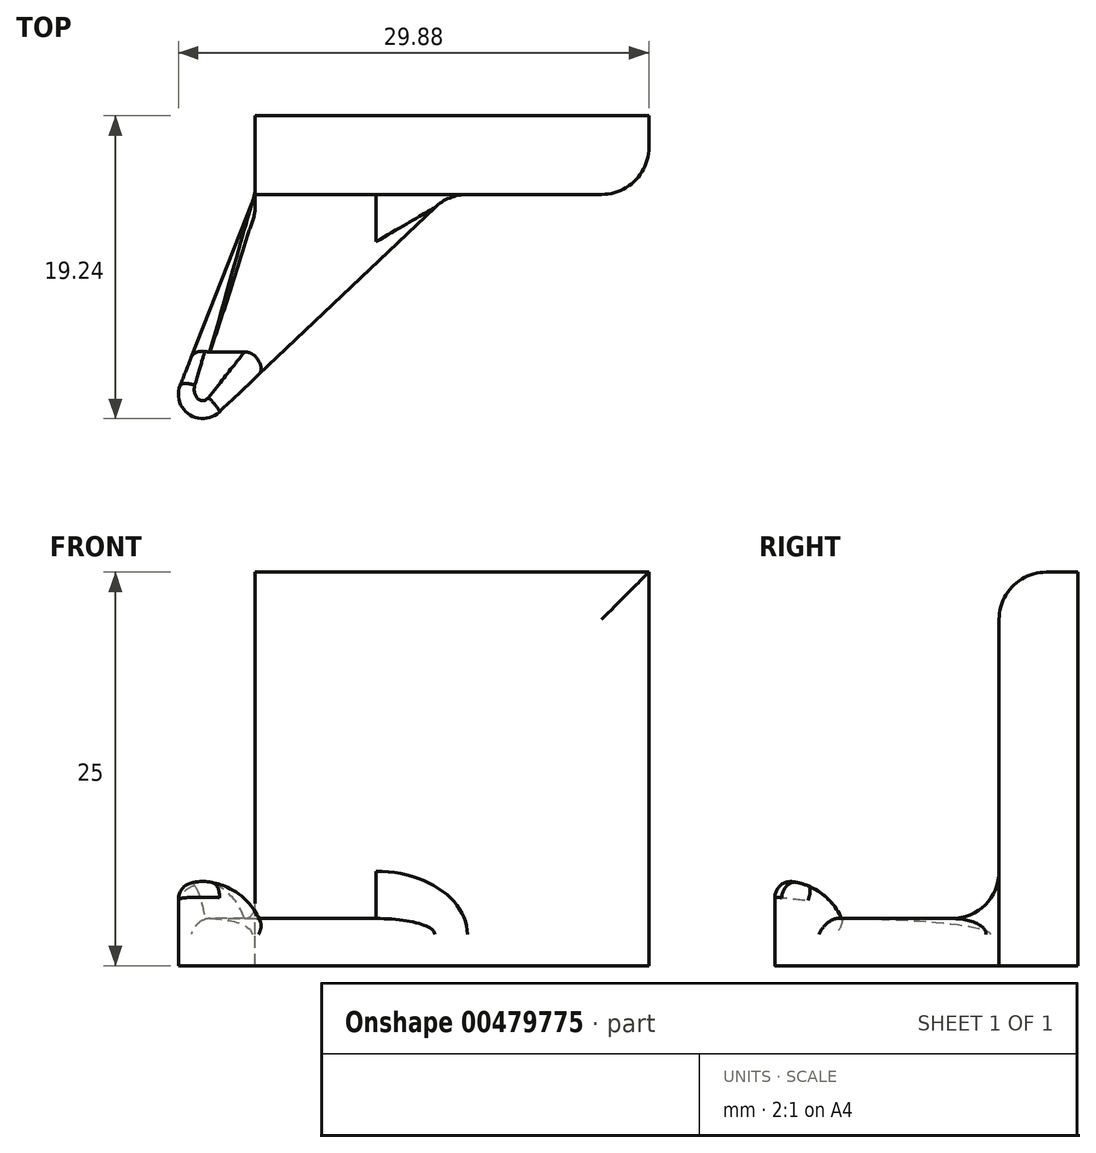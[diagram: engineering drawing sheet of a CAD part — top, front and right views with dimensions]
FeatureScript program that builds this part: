
annotation { "Feature Type Name" : "Feature", "Feature Type Description" : "" }
export const myFeature = defineFeature(function(context is Context, id is Id, definition is map)
    precondition{}
    {
        {
            var Q0;
            Q0=qCreatedBy(makeId("Front.planeOp"),FACE);
            var sketch = newSketch(context, id + "F0", { "sketchPlane" : qUnion([Q0])});
            skLineSegment(sketch, "E0.bottom", {"start": v(-12.27, 0) * mm, "end": v(12.73, 0) * mm});
            skLineSegment(sketch, "E0.top", {"start": v(-12.27, 25) * mm, "end": v(12.73, 25) * mm});
            skLineSegment(sketch, "E0.left", {"start": v(-12.27, 0) * mm, "end": v(-12.27, 25) * mm});
            skLineSegment(sketch, "E0.right", {"start": v(12.73, 0) * mm, "end": v(12.73, 25) * mm});
            skSolve(sketch);
        }
        {
            var Q0;
            Q0=makeQuery(id+"F0.imprint","IMPRINT",FACE,{"disambiguationData":[TD([[makeQuery(id+"F0.imprint","IMPRINT",EDGE,{"derivedFrom":sQuery(id+"F0.wireOp",EDGE,"E0.bottom")}),1.0]])]});
            extrude(context, id + "F1", {"entities" : qUnion([Q0]), "oppositeDirection" : true, "depth" : 5 * mm});
        }
        {
            var Q0;
            Q0=makeQuery(id+"F1.opExtrude","SWEPT_FACE",FACE,{"disambiguationData":[OSD([sQuery(id+"F0.wireOp",EDGE,"E0.bottom")])]});
            var sketch = newSketch(context, id + "F2", { "sketchPlane" : qUnion([Q0])});
            skLineSegment(sketch, "E1", {"start": v(-12.27, 0) * mm, "end": v(-17.04, 12.13) * mm});
            skLineSegment(sketch, "E2", {"start": v(-14.55, 13.81) * mm, "end": v(0, 0) * mm});
            skLineSegment(sketch, "E3", {"start": v(0, 0) * mm, "end": v(-12.27, 0) * mm});
            skArc(sketch, "E4", {"start": v(-17.04, 12.13) * mm, "mid": v(-16.47, 13.97) * mm, "end": v(-14.55, 13.81) * mm});
            skSolve(sketch);
        }
        {
            var Q0;
            Q0=makeQuery(id+"F2.imprint","IMPRINT",FACE,{"disambiguationData":[TD([[makeQuery(id+"F2.imprint","IMPRINT",EDGE,{"derivedFrom":sQuery(id+"F2.wireOp",EDGE,"E1")}),-1.0]])]});
            extrude(context, id + "F3", {"entities" : qUnion([Q0]), "operationType" : NewBodyOperationType.ADD, "oppositeDirection" : true, "depth" : 10 * mm});
        }
        {
            var Q0;
            Q0=qCreatedBy(makeId("Right.planeOp"),FACE);
            var sketch = newSketch(context, id + "F4", { "sketchPlane" : qUnion([Q0])});
            skLineSegment(sketch, "E5", {"start": v(0, 11.8) * mm, "end": v(0, 3) * mm});
            skLineSegment(sketch, "E6", {"start": v(0, 3) * mm, "end": v(-10, 3) * mm});
            skLineSegment(sketch, "E7", {"start": v(-10.78, 5.38) * mm, "end": v(-15.7, 5.38) * mm});
            skLineSegment(sketch, "E8", {"start": v(-15.7, 5.38) * mm, "end": v(-15.7, 11.74) * mm});
            skLineSegment(sketch, "E9", {"start": v(-15.7, 11.74) * mm, "end": v(0, 11.8) * mm});
            skLineSegment(sketch, "E10", {"start": v(-10, 3) * mm, "end": v(-10.78, 5.38) * mm});
            skSolve(sketch);
        }
        {
            var Q0;
            Q0=makeQuery(id+"F4.imprint","IMPRINT",FACE,{"disambiguationData":[TD([[makeQuery(id+"F4.imprint","IMPRINT",EDGE,{"derivedFrom":sQuery(id+"F4.wireOp",EDGE,"E5")}),-1.0]])]});
            extrude(context, id + "F5", {"entities" : qUnion([Q0]), "operationType" : NewBodyOperationType.REMOVE, "endBound" : BoundingType.THROUGH_ALL, "oppositeDirection" : true, "depth" : 25 * mm});
        }
        {
            var Q0;
            Q0=makeQuery(id+"F5.boolean.opBoolean","COPY",EDGE,{"derivedFrom":makeQuery(id+"F5.opExtrude","SWEPT_EDGE",EDGE,{"disambiguationData":[OSD([sQuery(id+"F4.wireOp",EDGE,"E7"),sQuery(id+"F4.wireOp",EDGE,"E10")])]})});
            fillet(context, id + "F6", {"entities" : qUnion([Q0]), "radius" : 4 * mm, "tangentPropagation" : true, "allowEdgeOverflow" : false});
        }
        {
            var Q0;
            Q0=makeQuery(id+"F5.boolean.opBoolean","INTERSECT",EDGE,{"derivedFrom":[makeQuery(id+"F3.opExtrude","SWEPT_FACE",FACE,{"disambiguationData":[OSD([sQuery(id+"F2.wireOp",EDGE,"E1")])]}),makeQuery(id+"F5.opExtrude","SWEPT_FACE",FACE,{"disambiguationData":[OSD([sQuery(id+"F4.wireOp",EDGE,"E6")])]})]});
            var Q1;
            Q1=makeQuery(id+"F5.boolean.opBoolean","INTERSECT",EDGE,{"derivedFrom":[makeQuery(id+"F3.opExtrude","SWEPT_FACE",FACE,{"disambiguationData":[OSD([sQuery(id+"F2.wireOp",EDGE,"E2")])]}),makeQuery(id+"F5.opExtrude","SWEPT_FACE",FACE,{"disambiguationData":[OSD([sQuery(id+"F4.wireOp",EDGE,"E6")])]})]});
            fillet(context, id + "F7", {"entities" : qUnion([Q0, Q1]), "radius" : 1 * mm, "tangentPropagation" : true, "allowEdgeOverflow" : false});
        }
        {
            var Q0;
            Q0=makeQuery(id+"F5.boolean.opBoolean","INTERSECT",EDGE,{"derivedFrom":[makeQuery(id+"F3.opExtrude","SWEPT_FACE",FACE,{"disambiguationData":[OSD([sQuery(id+"F2.wireOp",EDGE,"E4")])]}),makeQuery(id+"F5.opExtrude","SWEPT_FACE",FACE,{"disambiguationData":[OSD([sQuery(id+"F4.wireOp",EDGE,"E7")])]})]});
            var Q1;
            Q1=makeQuery(id+"F6.opFillet","BLEND_EDGE",EDGE,{"blendedFrom":[makeQuery(id+"F5.boolean.opBoolean","COPY",EDGE,{"derivedFrom":makeQuery(id+"F5.opExtrude","SWEPT_EDGE",EDGE,{"disambiguationData":[OSD([sQuery(id+"F4.wireOp",EDGE,"E7"),sQuery(id+"F4.wireOp",EDGE,"E10")])]})}),makeQuery(id+"F3.opExtrude","SWEPT_FACE",FACE,{"disambiguationData":[OSD([sQuery(id+"F2.wireOp",EDGE,"E4")])]})],"blendedInto":[makeQuery(id+"F3.opExtrude","SWEPT_FACE",FACE,{"disambiguationData":[OSD([sQuery(id+"F2.wireOp",EDGE,"E4")])]})]});
            var Q2;
            Q2=makeQuery(id+"F5.boolean.opBoolean","INTERSECT",EDGE,{"derivedFrom":[makeQuery(id+"F3.opExtrude","SWEPT_FACE",FACE,{"disambiguationData":[OSD([sQuery(id+"F2.wireOp",EDGE,"E2")])]}),makeQuery(id+"F5.opExtrude","SWEPT_FACE",FACE,{"disambiguationData":[OSD([sQuery(id+"F4.wireOp",EDGE,"E7")])]})]});
            fillet(context, id + "F8", {"entities" : qUnion([Q0, Q1, Q2]), "radius" : 1 * mm, "tangentPropagation" : true, "allowEdgeOverflow" : false});
        }
        {
            var Q0;
            Q0=makeQuery(id+"F1.opExtrude","CAP_EDGE",EDGE,{"disambiguationData":[OSD([sQuery(id+"F0.wireOp",EDGE,"E0.top")])],"isStart":true});
            var Q1;
            Q1=makeQuery(id+"F1.opExtrude","CAP_EDGE",EDGE,{"disambiguationData":[OSD([sQuery(id+"F0.wireOp",EDGE,"E0.right")])],"isStart":true});
            var Q2;
            {var subQ0=sQuery(id+"F0.wireOp",EDGE,"E0.left");var subQ1=makeQuery(id+"F1.opExtrude","CAP_EDGE",EDGE,{"disambiguationData":[OSD([subQ0])],"isStart":true});Q2=makeQuery(id+"F5.boolean.opBoolean","MERGE",EDGE,{"derivedFrom":[makeQuery(id+"F3.boolean.opBoolean","MERGE",EDGE,{"derivedFrom":[subQ1,makeQuery(id+"F3.opExtrude","SWEPT_EDGE",EDGE,{"disambiguationData":[OSD([sQuery(id+"F0.wireOp",EDGE,"E0.bottom"),subQ0,sQuery(id+"F2.wireOp",EDGE,"E1"),sQuery(id+"F2.wireOp",EDGE,"E3")])]})]}),makeQuery(id+"F3.boolean.opBoolean","SPLIT",EDGE,{"derivedFrom":subQ1})]});}
            fillet(context, id + "F9", {"entities" : qUnion([Q0, Q1, Q2]), "radius" : 3 * mm, "tangentPropagation" : true, "allowEdgeOverflow" : false});
        }
    });
